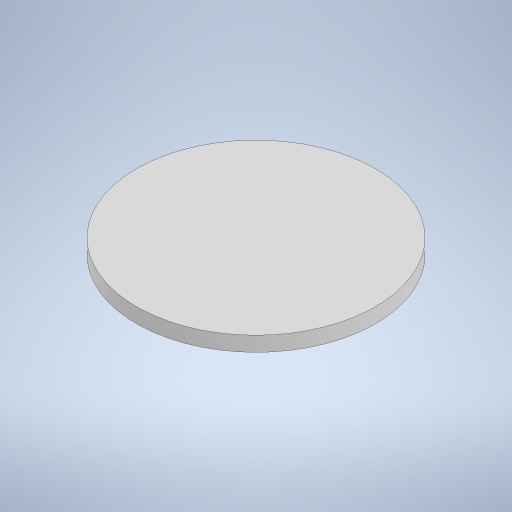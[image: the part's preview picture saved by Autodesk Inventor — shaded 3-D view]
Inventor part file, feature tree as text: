
AUTODESK INVENTOR PART (.ipt)
format: ipt  version: 2024.1 (Build 281209000, 209)  size: 362,496 bytes
history: native  units: in
note: dims shown in document units (in); Inventor stores cm internally (conversion verified against a paired STEP export)
features: sketch x3, extrude x2
ambient origin geometry x8: Origin, YZ Plane, XZ Plane, XY Plane, X Axis, Y Axis, Z Axis, Center Point
bodies: Solid1 (feature_tree)
feature tree (5):
  extrude  "Extrusion1"  Depth=0.062in TaperAngle=0.0deg
  extrude  "Extrusion2"  Depth=0.0787in
  sketch  "Sketch3"  dims[d5=0.0394in d6=0.0197in d7=0.0394in d8=0.0197in d9=0.0394in d10=0.0197in d11=0.0394in d12=0.0197in d13=0.0394in d14=0.0197in d15=0.0394in d16=0.0197in d17=0.0787in d18=0.0787in d19=0.0787in d20=0.0709in d21=0.0in d22=0.0787in d23=0.0197in d24=0.0197in d25=0.0394in d26=180.0deg d27=0.0197in d28=0.0394in d29=0.0197in d30=0.0394in d31=0.0197in d32=0.0394in d33=0.0197in d34=0.0394in d35=0.0197in]
  sketch  "Sketch1"  dims[d0=1.0in d1=0.062in d2=0.0in]
  sketch  "Sketch2"  dims[d3=0.73in d4=0.0787in]
